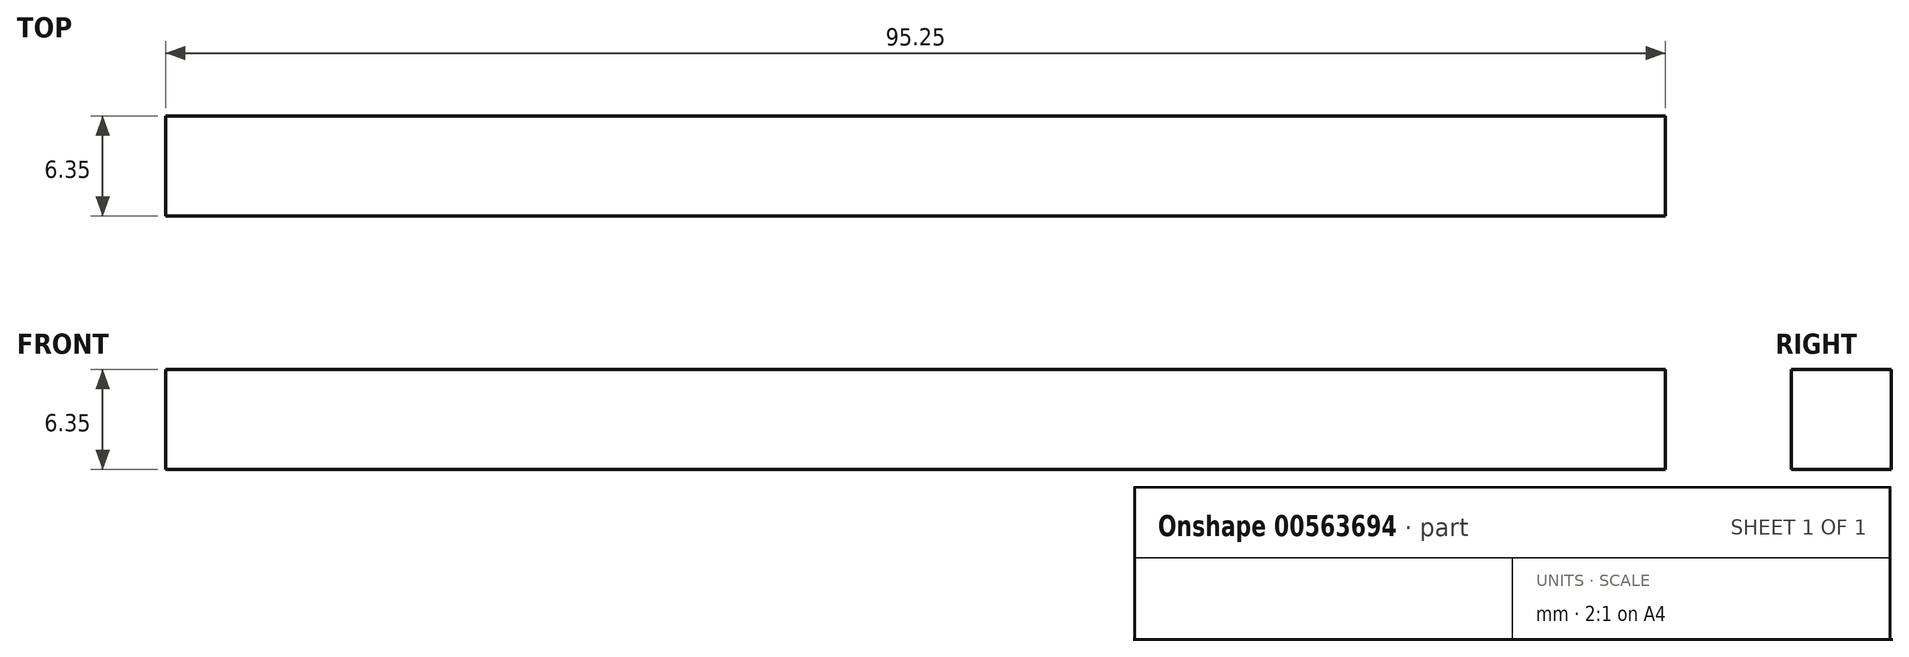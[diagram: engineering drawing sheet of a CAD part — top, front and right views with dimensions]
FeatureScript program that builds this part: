
annotation { "Feature Type Name" : "Feature", "Feature Type Description" : "" }
export const myFeature = defineFeature(function(context is Context, id is Id, definition is map)
    precondition{}
    {
        {
            var Q0;
            Q0=qCreatedBy(makeId("Front.planeOp"),FACE);
            var sketch = newSketch(context, id + "F0", { "sketchPlane" : qUnion([Q0])});
            skLineSegment(sketch, "E0.bottom", {"start": v(0, 0) * mm, "end": v(95.25, 0) * mm});
            skLineSegment(sketch, "E0.top", {"start": v(0, 6.35) * mm, "end": v(95.25, 6.35) * mm});
            skLineSegment(sketch, "E0.left", {"start": v(0, 0) * mm, "end": v(0, 6.35) * mm});
            skLineSegment(sketch, "E0.right", {"start": v(95.25, 0) * mm, "end": v(95.25, 6.35) * mm});
            skSolve(sketch);
        }
        {
            var Q0;
            Q0 = qSketchRegion(id + "F0", true);
            extrude(context, id + "F1", {"entities" : qUnion([Q0]), "depth" : 6.35 * mm, "offsetDistance" : 25.4 * mm});
        }
    });
